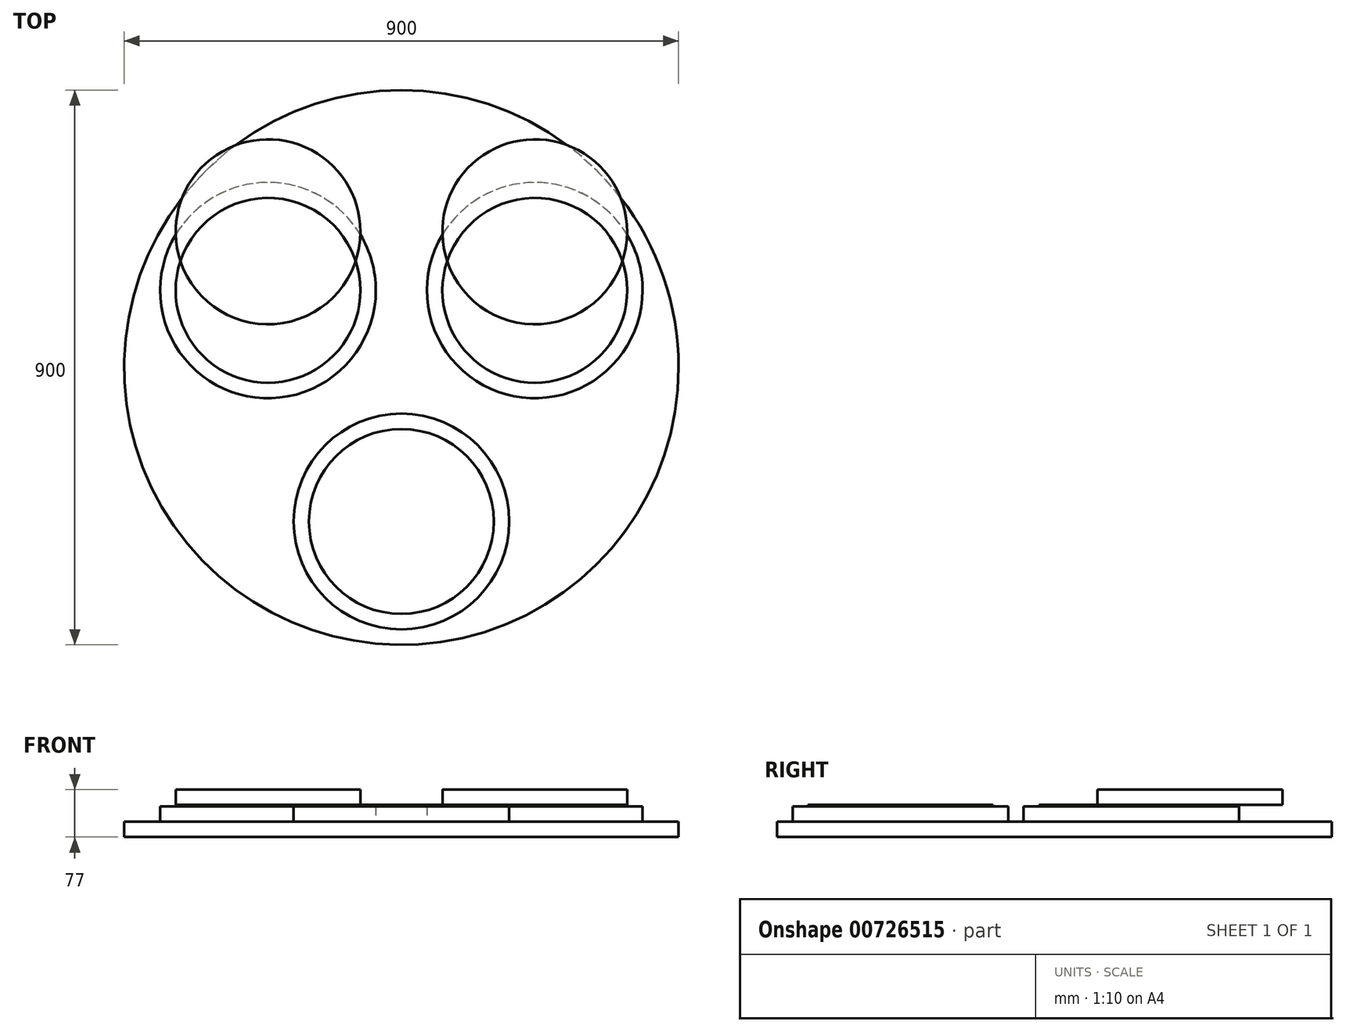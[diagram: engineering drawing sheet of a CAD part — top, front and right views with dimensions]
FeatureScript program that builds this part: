
annotation { "Feature Type Name" : "Feature", "Feature Type Description" : "" }
export const myFeature = defineFeature(function(context is Context, id is Id, definition is map)
    precondition{}
    {
        {
            var Q0;
            Q0=qCreatedBy(makeId("Top.planeOp"),FACE);
            var sketch = newSketch(context, id + "F0", { "sketchPlane" : qUnion([Q0])});
            skCircle(sketch, "E0", {"center": v(0, 0) * mm, "radius": 450 * mm});
            skSolve(sketch);
        }
        {
            var Q0;
            Q0=makeQuery(id+"F0.imprint","IMPRINT",FACE,{"disambiguationData":[TD([[makeQuery(id+"F0.imprint","IMPRINT",EDGE,{"derivedFrom":sQuery(id+"F0.wireOp",EDGE,"E0")}),1.0]])]});
            extrude(context, id + "F1", {"entities" : qUnion([Q0]), "depth" : 25 * mm, "offsetDistance" : 25 * mm});
        }
        {
            var Q0;
            Q0=makeQuery(id+"F1.opExtrude","CAP_FACE",FACE,{"disambiguationData":[OSD([sQuery(id+"F0.wireOp",EDGE,"E0")])],"isStart":false});
            var sketch = newSketch(context, id + "F2", { "sketchPlane" : qUnion([Q0])});
            skCircle(sketch, "E1", {"center": v(0, -250) * mm, "radius": 175 * mm});
            skCircle(sketch, "E2.1.0", {"center": v(216.5, 125) * mm, "radius": 175 * mm});
            skCircle(sketch, "E2.2.0", {"center": v(-216.5, 125) * mm, "radius": 175 * mm});
            skPoint(sketch, "E2.center", {"position": v(0, 0) * mm});
            skSolve(sketch);
        }
        {
            var Q0;
            Q0=makeQuery(id+"F2.imprint","IMPRINT",FACE,{"disambiguationData":[TD([[makeQuery(id+"F2.imprint","IMPRINT",EDGE,{"derivedFrom":sQuery(id+"F2.wireOp",EDGE,"E1")}),1.0]])]});
            var Q1;
            Q1=makeQuery(id+"F2.imprint","IMPRINT",FACE,{"disambiguationData":[TD([[makeQuery(id+"F2.imprint","IMPRINT",EDGE,{"derivedFrom":sQuery(id+"F2.wireOp",EDGE,"E2.2.0")}),1.0]])]});
            var Q2;
            Q2=makeQuery(id+"F2.imprint","IMPRINT",FACE,{"disambiguationData":[TD([[makeQuery(id+"F2.imprint","IMPRINT",EDGE,{"derivedFrom":sQuery(id+"F2.wireOp",EDGE,"E2.1.0")}),1.0]])]});
            extrude(context, id + "F3", {"entities" : qUnion([Q0, Q1, Q2]), "operationType" : NewBodyOperationType.ADD, "depth" : 25 * mm, "offsetDistance" : 25 * mm});
        }
        {
            var Q0;
            Q0=makeQuery(id+"F3.opExtrude","CAP_FACE",FACE,{"disambiguationData":[OSD([sQuery(id+"F2.wireOp",EDGE,"E2.2.0")])],"isStart":false});
            var sketch = newSketch(context, id + "F4", { "sketchPlane" : qUnion([Q0])});
            skCircle(sketch, "E3", {"center": v(-216.5, 125) * mm, "radius": 150 * mm});
            skCircle(sketch, "E4", {"center": v(0, -250) * mm, "radius": 150 * mm});
            skCircle(sketch, "E5", {"center": v(216.5, 125) * mm, "radius": 150 * mm});
            skSolve(sketch);
        }
        {
            var Q0;
            Q0=makeQuery(id+"F4.imprint","IMPRINT",FACE,{"disambiguationData":[TD([[makeQuery(id+"F4.imprint","IMPRINT",EDGE,{"derivedFrom":sQuery(id+"F4.wireOp",EDGE,"E3")}),1.0]])]});
            var Q1;
            Q1=makeQuery(id+"F4.imprint","IMPRINT",FACE,{"disambiguationData":[TD([[makeQuery(id+"F4.imprint","IMPRINT",EDGE,{"derivedFrom":sQuery(id+"F4.wireOp",EDGE,"E5")}),1.0]])]});
            var Q2;
            Q2=makeQuery(id+"F4.imprint","IMPRINT",FACE,{"disambiguationData":[TD([[makeQuery(id+"F4.imprint","IMPRINT",EDGE,{"derivedFrom":sQuery(id+"F4.wireOp",EDGE,"E4")}),1.0]])]});
            extrude(context, id + "F5", {"entities" : qUnion([Q0, Q1, Q2]), "operationType" : NewBodyOperationType.ADD, "depth" : 2 * mm, "offsetDistance" : 25 * mm});
        }
        {
            var Q0;
            Q0=makeQuery(id+"F5.opExtrude","CAP_FACE",FACE,{"disambiguationData":[OSD([sQuery(id+"F4.wireOp",EDGE,"E3")])],"isStart":false});
            var sketch = newSketch(context, id + "F6", { "sketchPlane" : qUnion([Q0])});
            skCircle(sketch, "E6", {"center": v(-216.5, 220) * mm, "radius": 150 * mm});
            skLineSegment(sketch, "E7", {"start": v(-216.5, 125) * mm, "end": v(-216.5, 201.23) * mm, "construction": true});
            skCircle(sketch, "E8", {"center": v(216.5, 220) * mm, "radius": 150 * mm});
            skSolve(sketch);
        }
        {
            var Q0;
            {var subQ0=sQuery(id+"F6.wireOp",EDGE,"E6");var subQ1=makeQuery(id+"F5.opExtrude","CAP_EDGE",EDGE,{"disambiguationData":[OSD([sQuery(id+"F4.wireOp",EDGE,"E3")])],"isStart":false});var subQ2=makeQuery(id+"F6.imprint","INTERSECT",VERTEX,{"disambiguationData":[OD(0.0)],"derivedFrom":[subQ1,subQ0]});Q0=makeQuery(id+"F6.imprint","IMPRINT",FACE,{"disambiguationData":[TD([[makeQuery(id+"F6.imprint","IMPRINT",EDGE,{"disambiguationData":[TD([[subQ2,1.0]])],"derivedFrom":subQ0}),1.0]])]});}
            var Q1;
            {var subQ0=sQuery(id+"F6.wireOp",EDGE,"E6");var subQ1=makeQuery(id+"F5.opExtrude","CAP_EDGE",EDGE,{"disambiguationData":[OSD([sQuery(id+"F4.wireOp",EDGE,"E3")])],"isStart":false});var subQ2=makeQuery(id+"F6.imprint","INTERSECT",VERTEX,{"disambiguationData":[OD(0.0)],"derivedFrom":[subQ1,subQ0]});Q1=makeQuery(id+"F6.imprint","IMPRINT",FACE,{"disambiguationData":[TD([[makeQuery(id+"F6.imprint","IMPRINT",EDGE,{"disambiguationData":[TD([[subQ2,-1.0]])],"derivedFrom":subQ0}),1.0]])]});}
            var Q2;
            Q2=makeQuery(id+"F6.imprint","IMPRINT",FACE,{"disambiguationData":[TD([[makeQuery(id+"F6.imprint","IMPRINT",EDGE,{"derivedFrom":sQuery(id+"F6.wireOp",EDGE,"E8")}),1.0]])]});
            extrude(context, id + "F7", {"entities" : qUnion([Q0, Q1, Q2]), "operationType" : NewBodyOperationType.ADD, "depth" : 25 * mm, "offsetDistance" : 25 * mm});
        }
    });
